# Revit family: Hager-Univers-IP54-D205-H1250-Cl.II-Encl-CH-fr
name_source: partatom
category: Equipement électrique
units: mm (PartAtom-declared; Revit-internal decimal feet)

## family parameters
Configuration du panneau = Deux colonnes, circuits au sein
Cote de connecteur circulaire = Utiliser le diamètre
Couper avec des vides une fois chargée = Non
Hôte = Face
Partagée = Non
Point de calcul de pièce = Non
Type d'élément = Tableau de raccordement

## types (5) — shared parameters
Commentaires du type = Univers
EF000003 - mode de pose = EV000384 - saillie
EF000007 - couleur = EV000202 - blanc
EF000040 - hauteur = 1250 mm  [stored 4.10105 ft]
EF000049 - profondeur = 205 mm  [stored 0.672572 ft]
EF000116 - numéro RAL = 9010
EF000118 - avec cadre/support de montage = Non
EF000266 - nombre de rangées = 8
EF001088 - possibilité de montage en saillie = Oui
EF001596 - matériau du boîtier/corps = EV000179 - acier
EF001613 - maintien de fonction = EV000494 - sans
EF003532 - convient pour utilisation à l’extérieur = Non
EF004293 - indice de protection contre les chocs (IK) = EV006815 - IK09
EF005474 - indice de protection (IP) = EV006419 - IP54
EF006244 - couvercle/porte transparent(e) = Non
EF006306 - avec serrure = Non
EF007800 - adapté à un parafoudre = Non
EF008873 - courant nominal (In) = 250 A
EF009170 - épaisseur de matériau du boîtier = 1 mm  [stored 0.00328084 ft]
EF009171 - épaisseur de matériau de la porte/du couvercle = 1 mm  [stored 0.00328084 ft]
EF009212 - finition du couvercle = EV000116 - fermé
EF015940 - couvercle avec décharge de pression = Non
Fabricant = Hager
HG000002 - avec porte = Oui
HG000003 - Gamme = Univers
HG000006 - Encastré = Non
HG000010 - Portes asymétriques = Non
HG000023 - Armoire double section = Non
HG000024 - Hauteur de la section basse = 800 mm  [stored 2.62467 ft]
HG000026 - Installation au sol = Non
zero-valued in all types: EF000218 - profondeur d'encastrement, Elévation par défaut, HG000027 - Hauteur du socle

## per-type parameters (varying)
| type | EF000008 - largeur | EF000339 - type de capot | EF000437 - nombre d'entrées de conduit | EF001131 - profondeur intérieure | EF002950 - largeur en nombre de modules | EF004427 - nombre de modules | EF004464 - type de porte | EF009554 - nombre d'ouvertures pour plaques à bride | HG000004 - Référence fabricant | HG000009 - Porte à double battant |
| saillie IP54 L1050 H1250 P205  - FP84QSW | 1050 mm | EV001012 - couvercle | 8 | 143 mm | 48 | 384 | EV003602 - double | 8 | FP84QSW | Oui |
| saillie IP54 L1300 H1250 P205  - FP85QSW | 1300 mm  [stored 4.26509 ft] | EV004216 - porte | 10 | 130 mm  [stored 0.426509 ft] | 60 | 480 | EV003602 - double | 10 | FP85QSW | Non |
| saillie IP54 L300 H1250 P205  - FP81QSW | 300 mm | EV004216 - porte | 2 | 130 mm  [stored 0.426509 ft] | 12 | 96 | EV002646 - unique | 2 | FP81QSW | Non |
| saillie IP54 L550 H1250 P205  - FP82QSW | 550 mm | EV004216 - porte | 4 | 130 mm  [stored 0.426509 ft] | 24 | 192 | EV002646 - unique | 4 | FP82QSW | Non |
| saillie IP54 L800 H1250 P205  - FP83QSW | 800 mm  [stored 2.62467 ft] | EV001012 - couvercle | 6 | 143 mm | 36 | 288 | EV002646 - unique | 6 | FP83QSW | Non |

note: [stored X ft] marks values corroborated as IEEE doubles in the binary element streams (Revit-internal decimal feet)

## geometry (parser evidence)
native form markers: Sweep x10
no freeform markers — native parametric forms only
